# Revit family: Sanitary_Mirrors_hansgrohe_54007CHN-CubeStack-Mirror-cabinet-800-16_1
name_source: partatom
category: Furniture
revit_build: Autodesk Revit 2018 (Build: 20170223_1515(x64)
units: mm (PartAtom-declared; Revit-internal decimal feet)

## family parameters
Always vertical = No
Cut with Voids When Loaded = No
OmniClass Number = 23.40.00.00
OmniClass Title = Equipment and Furnishings
Room Calculation Point = No
Shared = No
Work Plane-Based = Yes

## types (1)
- 477 Agategrey
    Always visible = Yes
    Apparent Load = 0 VA
    BIMobject category = Mirrors
    Connector Description = Power Supply
    Default Elevation = 1219.2 mm  [stored 4 ft]
    Description = CubeStack Mirror cabinet 800/160
    Design country = Germany
    EAN code = 4059625328668
    Edition number = 1
    GTIN code = https://4059625328668
    IFC Classification = Furnishing Element
    Manufacturer = hansgrohe
    Manufacturer country = Germany
    Manufacturer name = hansgrohe
    Material 1 = Hansgrohe - Wood - 477 Agategrey
    Material 2 = Hansgrohe - Glass - LED light
    Material 3 = Hansgrohe - Glass - Mirror
    Model = 54007CHN
    NBS Reference Code = 35-75-08
    NBS Reference Description = Bathroom Cabinets
    OmniClass Code = 23-31 25 13
    OmniClass Description = Bathroom Cabinets
    Power Factor = 1
    Power Supply = 220 V
    Product Guid = 741b44a8-c705-4b86-ac51-11988b5295fb
    Product SKU = 54007CHN
    Product data url = https://bimobject.com
    Product family = CubeStack
    Product group = mirror cabinet
    Product name = 54007CHN CubeStack Mirror cabinet 800/160
    QR code = https://bimobject.com
    URL = https://www.hansgrohe.com
    Uniclass 2015 Code = Pr_40_30_78_03
    Uniclass 2015 Name = Bathroom cabinets
    Uniformat II Code = E2010
    Uniformat II Description = Fixed Furnishings

note: [stored X ft] marks values corroborated as IEEE doubles in the binary element streams (Revit-internal decimal feet)

## geometry (parser evidence)
native form markers: Sweep x1
no freeform markers — native parametric forms only
